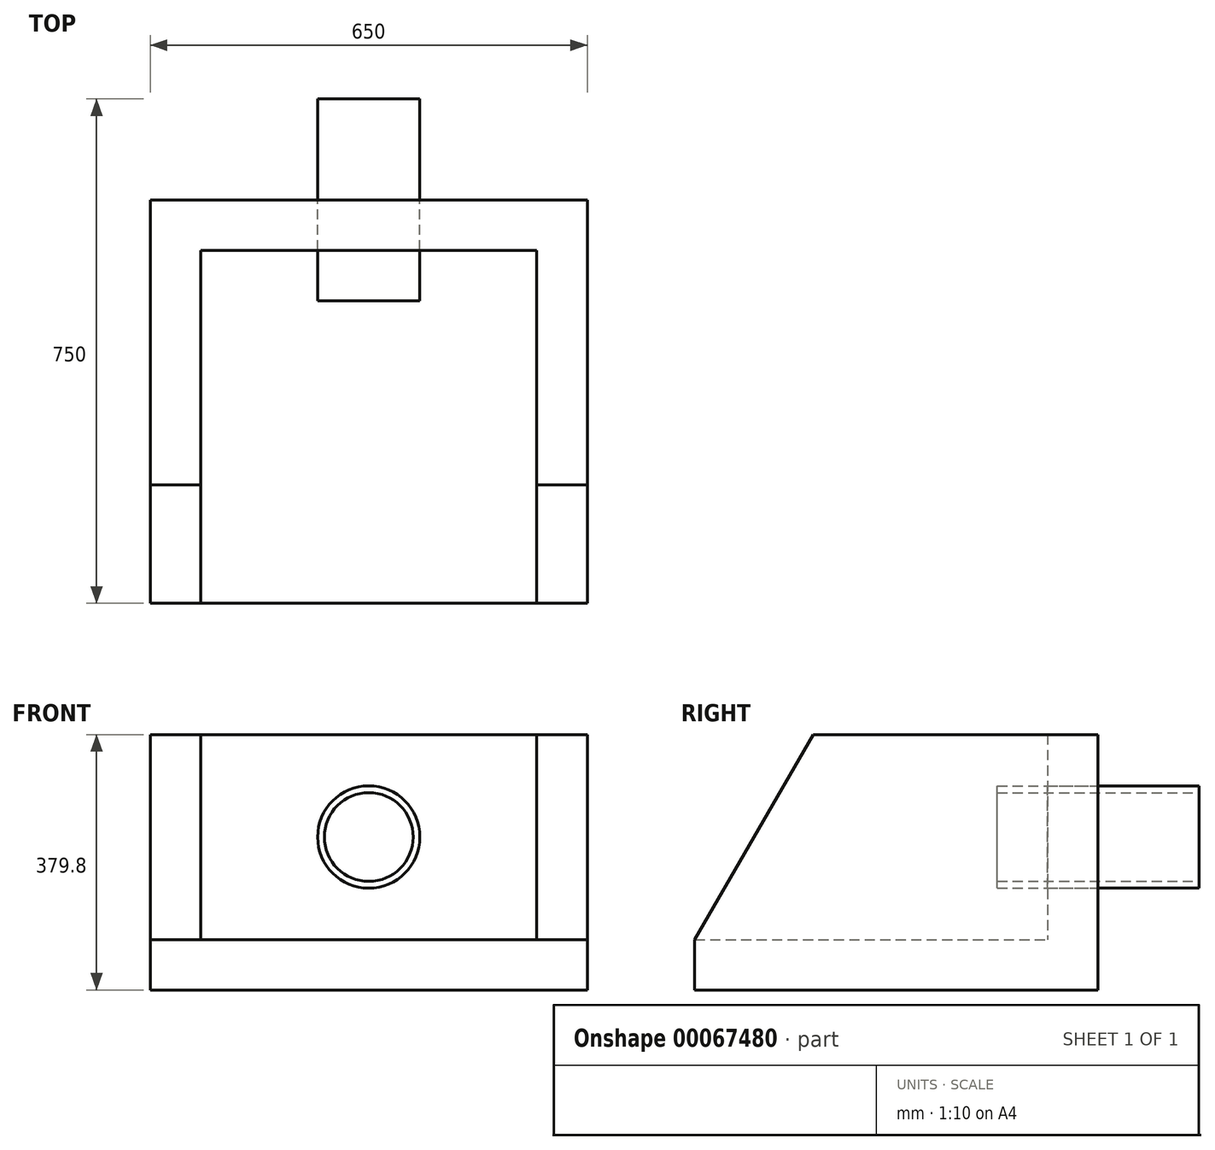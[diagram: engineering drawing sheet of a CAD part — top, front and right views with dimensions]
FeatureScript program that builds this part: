
annotation { "Feature Type Name" : "Feature", "Feature Type Description" : "" }
export const myFeature = defineFeature(function(context is Context, id is Id, definition is map)
    precondition{}
    {
        {
            var Q0;
            Q0=qCreatedBy(makeId("Front.planeOp"),FACE);
            var sketch = newSketch(context, id + "F0", { "sketchPlane" : qUnion([Q0])});
            skCircle(sketch, "E0", {"center": v(0, 0) * mm, "radius": 76 * mm});
            skCircle(sketch, "E1.0", {"center": v(0, 0) * mm, "radius": 66 * mm});
            skLineSegment(sketch, "E2.bottom", {"start": v(250, 152.4) * mm, "end": v(-250, 152.4) * mm});
            skLineSegment(sketch, "E2.top", {"start": v(250, -152.4) * mm, "end": v(-250, -152.4) * mm});
            skLineSegment(sketch, "E2.left", {"start": v(250, 152.4) * mm, "end": v(250, -152.4) * mm});
            skLineSegment(sketch, "E2.right", {"start": v(-250, 152.4) * mm, "end": v(-250, -152.4) * mm});
            skLineSegment(sketch, "E3.0", {"start": v(325, 152.4) * mm, "end": v(325, -227.4) * mm});
            skLineSegment(sketch, "E3.1", {"start": v(325, -227.4) * mm, "end": v(-325, -227.4) * mm});
            skLineSegment(sketch, "E3.2", {"start": v(-325, 152.4) * mm, "end": v(-325, -227.4) * mm});
            skLineSegment(sketch, "E4", {"start": v(-250, 152.4) * mm, "end": v(-325, 152.4) * mm});
            skLineSegment(sketch, "E5", {"start": v(325, 152.4) * mm, "end": v(250, 152.4) * mm});
            skSolve(sketch);
        }
        {
            var Q0;
            Q0=makeQuery(id+"F0.imprint","IMPRINT",FACE,{"disambiguationData":[TD([[makeQuery(id+"F0.imprint","IMPRINT",EDGE,{"derivedFrom":sQuery(id+"F0.wireOp",EDGE,"E0")}),-1.0]])]});
            extrude(context, id + "F1", {"entities" : qUnion([Q0]), "depth" : 75 * mm});
        }
        {
            var Q0;
            Q0=makeQuery(id+"F0.imprint","IMPRINT",FACE,{"disambiguationData":[TD([[makeQuery(id+"F0.imprint","IMPRINT",EDGE,{"derivedFrom":sQuery(id+"F0.wireOp",EDGE,"E0")}),1.0]])]});
            extrude(context, id + "F2", {"entities" : qUnion([Q0]), "endBound" : BoundingType.SYMMETRIC, "depth" : 300 * mm});
        }
        {
            var Q0;
            Q0=makeQuery(id+"F0.imprint","IMPRINT",FACE,{"disambiguationData":[TD([[makeQuery(id+"F0.imprint","IMPRINT",EDGE,{"derivedFrom":sQuery(id+"F0.wireOp",EDGE,"E2.top")}),1.0]])]});
            extrude(context, id + "F3", {"entities" : qUnion([Q0]), "operationType" : NewBodyOperationType.ADD, "depth" : 600 * mm});
        }
        {
            var Q0;
            Q0=makeQuery(id+"F3.opExtrude","SWEPT_FACE",FACE,{"disambiguationData":[OSD([sQuery(id+"F0.wireOp",EDGE,"E3.0")])]});
            var sketch = newSketch(context, id + "F4", { "sketchPlane" : qUnion([Q0])});
            skPoint(sketch, "E6.0", {"position": v(-600, -152.4) * mm});
            skLineSegment(sketch, "E7", {"start": v(-600, -152.4) * mm, "end": v(-424.02, 152.4) * mm});
            skLineSegment(sketch, "E8", {"start": v(-424.02, 152.4) * mm, "end": v(-600, 152.4) * mm});
            skLineSegment(sketch, "E9", {"start": v(-600, 152.4) * mm, "end": v(-600, -152.4) * mm});
            skLineSegment(sketch, "E10", {"start": v(-600, -152.4) * mm, "end": v(-510.88, -152.4) * mm, "construction": true});
            skSolve(sketch);
        }
        {
            var Q0;
            Q0=makeQuery(id+"F4.imprint","IMPRINT",FACE,{"disambiguationData":[TD([[makeQuery(id+"F4.imprint","IMPRINT",EDGE,{"derivedFrom":sQuery(id+"F4.wireOp",EDGE,"E7")}),1.0]])]});
            extrude(context, id + "F5", {"entities" : qUnion([Q0]), "operationType" : NewBodyOperationType.REMOVE, "endBound" : BoundingType.THROUGH_ALL, "oppositeDirection" : true, "depth" : 25 * mm});
        }
    });
